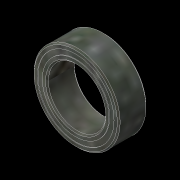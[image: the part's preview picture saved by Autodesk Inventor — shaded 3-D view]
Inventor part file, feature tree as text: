
AUTODESK INVENTOR PART (.ipt)
format: ipt  version: 2016 (Build 200138000, 138)  size: 604,160 bytes
history: native  units: in
note: dims shown in document units (in); Inventor stores cm internally (conversion verified against a paired STEP export)
features: other x11, revolve x5
ambient origin geometry x8: Origin, YZ Plane, XZ Plane, XY Plane, X Axis, Y Axis, Z Axis, Center Point
bodies: Solid1 (feature_tree), Solid2 (feature_tree), Solid3 (feature_tree), Solid4 (feature_tree), Solid5 (feature_tree), Solid6 (feature_tree), Solid7 (feature_tree), Solid8 (feature_tree), Solid9 (feature_tree), Solid10 (feature_tree), Solid11 (feature_tree), Solid12 (feature_tree), Solid13 (feature_tree), Solid14 (feature_tree), Solid15 (feature_tree), Solid16 (feature_tree)
feature tree (16):
  revolve  "Revolve1"  [1 undecoded]
  revolve  "Revolve3"  [1 undecoded]
  revolve  "Revolve4"  [1 undecoded]
  other  "CirPattern1[1]"
  other  "CirPattern1[2]"
  other  "CirPattern1[3]"
  other  "CirPattern1[4]"
  other  "CirPattern1[5]"
  other  "CirPattern1[6]"
  other  "CirPattern1[7]"
  other  "CirPattern1[8]"
  other  "CirPattern1[9]"
  other  "CirPattern1[10]"
  other  "CirPattern1[11]"
  revolve  "Revolve5[1]"  [1 undecoded]
  revolve  "Revolve5[2]"  [1 undecoded]
note: 5 required parameter values undecoded (feature->parameter linkage not recoverable at this tier; creation-order binding heuristic only, values carry confidence <= 0.55)
